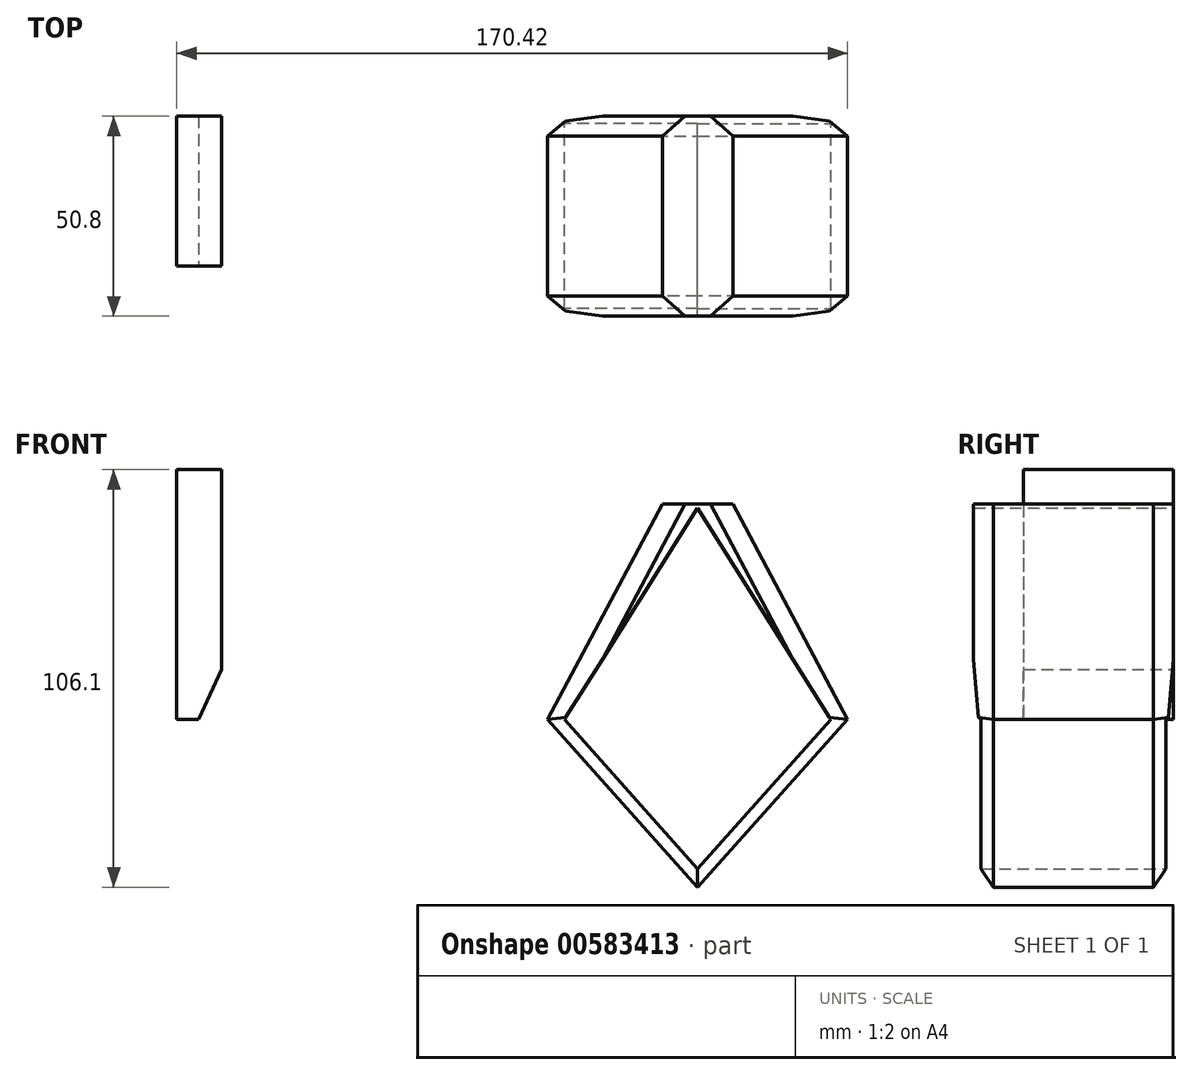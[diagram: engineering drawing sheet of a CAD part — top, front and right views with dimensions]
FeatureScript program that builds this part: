
annotation { "Feature Type Name" : "Feature", "Feature Type Description" : "" }
export const myFeature = defineFeature(function(context is Context, id is Id, definition is map)
    precondition{}
    {
        {
            var Q0;
            Q0=qCreatedBy(makeId("Front.planeOp"),FACE);
            var sketch = newSketch(context, id + "F0", { "sketchPlane" : qUnion([Q0])});
            skLineSegment(sketch, "E0", {"start": v(0, 0) * mm, "end": v(0, 71.7) * mm, "construction": true});
            skLineSegment(sketch, "E1", {"start": v(0, 71.7) * mm, "end": v(38.1, 0) * mm});
            skLineSegment(sketch, "E2", {"start": v(38.1, 0) * mm, "end": v(-38.1, 0) * mm});
            skLineSegment(sketch, "E3", {"start": v(-38.1, 0) * mm, "end": v(0, 71.7) * mm});
            skLineSegment(sketch, "E4", {"start": v(0, 0) * mm, "end": v(0, -42.6) * mm, "construction": true});
            skLineSegment(sketch, "E5", {"start": v(0, -42.6) * mm, "end": v(38.1, 0) * mm});
            skLineSegment(sketch, "E6", {"start": v(0, -42.6) * mm, "end": v(-38.1, 0) * mm});
            skLineSegment(sketch, "E7", {"start": v(0, -37.86) * mm, "end": v(-33.87, 0) * mm});
            skLineSegment(sketch, "E8", {"start": v(-33.87, 0) * mm, "end": v(0, 53.71) * mm});
            skLineSegment(sketch, "E9", {"start": v(0, 53.71) * mm, "end": v(33.87, 0) * mm});
            skLineSegment(sketch, "E10", {"start": v(33.87, 0) * mm, "end": v(0, -37.86) * mm});
            skLineSegment(sketch, "E11", {"start": v(0, 53.71) * mm, "end": v(0, 65.5) * mm});
            skSolve(sketch);
        }
        {
            var Q0;
            Q0 = qSketchRegion(id + "F0", true);
            extrude(context, id + "F1", {"entities" : qUnion([Q0]), "depth" : 50.8 * mm, "offsetDistance" : 25.4 * mm});
        }
        {
            var Q0;
            Q0=makeQuery(id+"F1.opExtrude","CAP_EDGE",EDGE,{"disambiguationData":[OSD([sQuery(id+"F0.wireOp",EDGE,"E6")])],"isStart":false});
            var Q1;
            Q1=makeQuery(id+"F1.opExtrude","CAP_EDGE",EDGE,{"disambiguationData":[OSD([sQuery(id+"F0.wireOp",EDGE,"E5")])],"isStart":false});
            var Q2;
            Q2=makeQuery(id+"F1.opExtrude","CAP_EDGE",EDGE,{"disambiguationData":[OSD([sQuery(id+"F0.wireOp",EDGE,"E3")])],"isStart":false});
            var Q3;
            Q3=makeQuery(id+"F1.opExtrude","CAP_EDGE",EDGE,{"disambiguationData":[OSD([sQuery(id+"F0.wireOp",EDGE,"E1")])],"isStart":false});
            var Q4;
            Q4=makeQuery(id+"F1.opExtrude","CAP_EDGE",EDGE,{"disambiguationData":[OSD([sQuery(id+"F0.wireOp",EDGE,"E6")])],"isStart":true});
            var Q5;
            Q5=makeQuery(id+"F1.opExtrude","CAP_EDGE",EDGE,{"disambiguationData":[OSD([sQuery(id+"F0.wireOp",EDGE,"E3")])],"isStart":true});
            var Q6;
            Q6=makeQuery(id+"F1.opExtrude","CAP_EDGE",EDGE,{"disambiguationData":[OSD([sQuery(id+"F0.wireOp",EDGE,"E5")])],"isStart":true});
            var Q7;
            Q7=makeQuery(id+"F1.opExtrude","CAP_EDGE",EDGE,{"disambiguationData":[OSD([sQuery(id+"F0.wireOp",EDGE,"E1")])],"isStart":true});
            chamfer(context, id + "F2", {"entities" : qUnion([Q0, Q1, Q2, Q3, Q4, Q5, Q6, Q7]), "width" : 5.08 * mm, "tangentPropagation" : true});
        }
        {
            var Q0;
            Q0=makeQuery(id+"F1.opExtrude","SWEPT_EDGE",EDGE,{"disambiguationData":[OSD([sQuery(id+"F0.wireOp",EDGE,"E1"),sQuery(id+"F0.wireOp",EDGE,"E3")])]});
            chamfer(context, id + "F3", {"entities" : qUnion([Q0]), "width" : 10.16 * mm, "tangentPropagation" : true});
        }
        {
            var Q0;
            Q0=qCreatedBy(makeId("Front.planeOp"),FACE);
            var sketch = newSketch(context, id + "F4", { "sketchPlane" : qUnion([Q0])});
            skLineSegment(sketch, "E12.bottom", {"start": v(-132.32, 63.5) * mm, "end": v(-120.9, 63.5) * mm});
            skLineSegment(sketch, "E12.top", {"start": v(-132.32, 0) * mm, "end": v(-120.9, 0) * mm});
            skLineSegment(sketch, "E12.left", {"start": v(-132.32, 63.5) * mm, "end": v(-132.32, 0) * mm});
            skLineSegment(sketch, "E12.right", {"start": v(-120.9, 63.5) * mm, "end": v(-120.9, 0) * mm});
            skSolve(sketch);
        }
        {
            var Q0;
            Q0 = qSketchRegion(id + "F4", true);
            extrude(context, id + "F5", {"entities" : qUnion([Q0]), "depth" : 38.1 * mm, "offsetDistance" : 25.4 * mm});
        }
        {
            var Q0;
            Q0=makeQuery(id+"F5.opExtrude","SWEPT_EDGE",EDGE,{"disambiguationData":[OSD([sQuery(id+"F4.wireOp",EDGE,"E12.top"),sQuery(id+"F4.wireOp",EDGE,"E12.right")])]});
            chamfer(context, id + "F6", {"entities" : qUnion([Q0]), "chamferType" : ChamferType.OFFSET_ANGLE, "width" : 12.7 * mm, "oppositeDirection" : false, "angle" : 25 * degree, "tangentPropagation" : true});
        }
        {
            var Q0;
            Q0=qCreatedBy(makeId("Front.planeOp"),FACE);
            var sketch = newSketch(context, id + "F7", { "sketchPlane" : qUnion([Q0])});
            skLineSegment(sketch, "E13.bottom", {"start": v(133.37, 0) * mm, "end": v(121.94, 0) * mm});
            skLineSegment(sketch, "E13.top", {"start": v(133.37, 63.5) * mm, "end": v(121.94, 63.5) * mm});
            skLineSegment(sketch, "E13.left", {"start": v(133.37, 0) * mm, "end": v(133.37, 63.5) * mm});
            skLineSegment(sketch, "E13.right", {"start": v(121.94, 0) * mm, "end": v(121.94, 63.5) * mm});
            skSolve(sketch);
        }
        {
            var Q0;
            Q0 = qSketchRegion(id + "F7", true);
            extrude(context, id + "F8", {"entities" : qUnion([Q0]), "depth" : 50.8 * mm, "offsetDistance" : 25.4 * mm});
        }
        {
            var Q0;
            Q0=makeQuery(id+"F8.opExtrude","SWEPT_EDGE",EDGE,{"disambiguationData":[OSD([sQuery(id+"F7.wireOp",EDGE,"E13.bottom"),sQuery(id+"F7.wireOp",EDGE,"E13.right")])]});
            chamfer(context, id + "F9", {"entities" : qUnion([Q0]), "chamferType" : ChamferType.OFFSET_ANGLE, "width" : 5.08 * mm, "oppositeDirection" : false, "angle" : 70 * degree, "tangentPropagation" : true});
        }
        {
            var Q0;
            Q0=makeQuery(id+"F8.opExtrude","SWEPT_BODY",BODY,{"disambiguationData":[OSD([sQuery(id+"F7.wireOp",EDGE,"E13.bottom"),sQuery(id+"F7.wireOp",EDGE,"E13.top"),sQuery(id+"F7.wireOp",EDGE,"E13.left"),sQuery(id+"F7.wireOp",EDGE,"E13.right")])]});
            deleteBodies(context, id + "F10", {"entities" : qUnion([Q0])});
        }
    });
